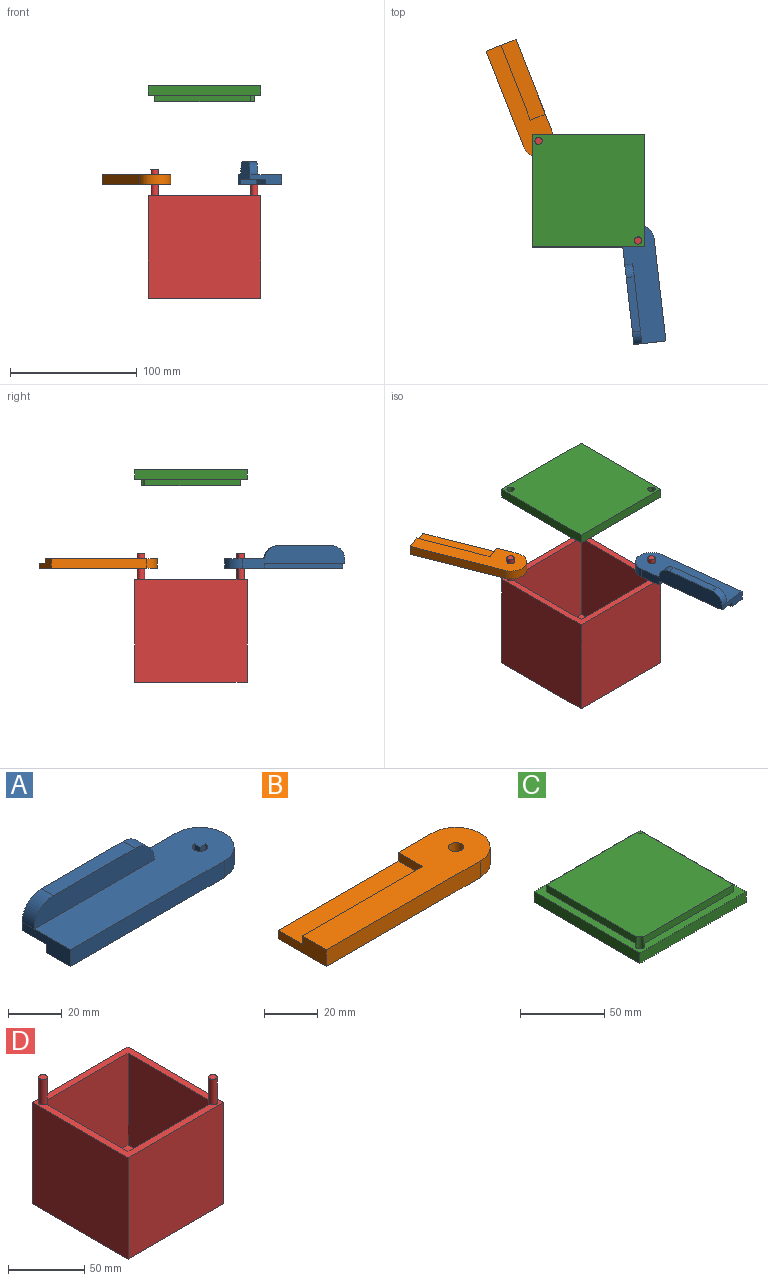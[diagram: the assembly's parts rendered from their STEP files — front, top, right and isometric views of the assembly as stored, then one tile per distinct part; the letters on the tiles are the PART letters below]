
ASSEMBLY  parts=4 mates=3
PART A: 16 faces, bbox 94x25.4x17.8 mm
  f0: plane 25.4x7.62mm, normal (-1,0,0), area 145.2mm2, adj f3,f4,f5,f6,f11,f13,f14
  f1: plane 63.5x10.16mm, normal (0,-1,0), area 600.9mm2, adj f2,f3,f14,f15
  f2: plane 43.18x6.35mm, normal (0,0,1), area 274.2mm2, adj f1,f4,f14,f15
  f3: plane 93.98x25.4mm, normal (0,0,1), area 1895.2mm2, adj f0,f1,f4,f5,f7,f8,f9,f10
  f4: plane 81.28x17.78mm, normal (0,1,0), area 978.3mm2, adj f0,f2,f3,f6,f7,f11,f12,f14
  f5: plane 81.28x7.62mm, normal (0,-1,0), area 619.4mm2, adj f0,f3,f6,f7
  f6: plane 93.98x25.4mm, normal (0,0,-1), area 1492mm2, adj f0,f4,f5,f7,f8,f9,f10,f12
  f7: cylinder r=12.7mm len=25.4mm, axis (0,0,1), area 304mm2, adj f3,f4,f5,f6
  f8: plane 7.62x2.87mm, normal (-1,0,0), area 21.9mm2, adj f3,f6,f9,f10
  f9: cylinder r=2.87mm len=7.62mm, axis (0,0,1), area 103.1mm2, adj f3,f6,f8,f10
  f10: plane 7.62x2.87mm, normal (0,-1,0), area 21.9mm2, adj f3,f6,f8,f9
  f11: plane 63.5x12.7mm, normal (0,0,-1), area 806.4mm2, adj f0,f4,f12,f13
  f12: plane 12.7x3.81mm, normal (-1,0,0), area 48.4mm2, adj f4,f6,f11,f13
  f13: plane 63.5x3.81mm, normal (0,1,0), area 241.9mm2, adj f0,f6,f11,f12
  f14: cylinder r=10.16mm len=10.16mm, axis (0,1,0), area 101.3mm2, adj f0,f1,f2,f4
  f15: cylinder r=10.16mm len=10.16mm, axis (0,1,0), area 101.3mm2, adj f1,f2,f3,f4
PART B: 10 faces, bbox 94x25.4x7.6 mm
  f0: plane 25.4x7.62mm, normal (-1,0,0), area 145.2mm2, adj f1,f2,f3,f4,f7,f9
  f1: plane 93.98x25.4mm, normal (0,0,1), area 1485.5mm2, adj f0,f2,f3,f5,f6,f8,f9
  f2: plane 81.28x7.62mm, normal (0,-1,0), area 619.4mm2, adj f0,f1,f4,f5
  f3: plane 81.28x7.62mm, normal (0,1,0), area 377.4mm2, adj f0,f1,f4,f5,f7,f8
  f4: plane 93.98x25.4mm, normal (0,0,-1), area 2291.9mm2, adj f0,f2,f3,f5,f6
  f5: cylinder r=12.7mm len=25.4mm, axis (0,0,1), area 304mm2, adj f1,f2,f3,f4
  f6: cylinder r=2.87mm len=7.62mm, axis (0,0,1), area 137.6mm2, adj f1,f4
  f7: plane 63.5x12.7mm, normal (0,0,1), area 806.4mm2, adj f0,f3,f8,f9
  f8: plane 12.7x3.81mm, normal (-1,0,0), area 48.4mm2, adj f1,f3,f7,f9
  f9: plane 63.5x3.81mm, normal (0,1,0), area 241.9mm2, adj f0,f1,f7,f8
PART C: 13 faces, bbox 88.9x88.9x12.7 mm
  f0: plane 88.9x88.9mm, normal (0,0,1), area 1664.4mm2, adj f1,f2,f3,f4,f6,f7,f8,f9
  f1: plane 88.9x7.62mm, normal (1,0,0), area 677.4mm2, adj f0,f2,f4,f5
  f2: plane 88.9x7.62mm, normal (0,1,0), area 677.4mm2, adj f0,f1,f3,f5
  f3: plane 88.9x7.62mm, normal (-1,0,0), area 677.4mm2, adj f0,f2,f4,f5
  f4: plane 88.9x7.62mm, normal (0,-1,0), area 677.4mm2, adj f0,f1,f3,f5
  f5: plane 88.9x88.9mm, normal (0,0,-1), area 7851.4mm2, adj f1,f2,f3,f4,f11,f12
  f6: plane 75.87x5.08mm, normal (0,-1,0), area 385.4mm2, adj f0,f7,f10,f11
  f7: plane 75.87x5.08mm, normal (1,0,0), area 385.4mm2, adj f0,f6,f10,f12
  f8: plane 75.87x5.08mm, normal (0,1,0), area 385.4mm2, adj f0,f9,f10,f12
  f9: plane 75.87x5.08mm, normal (-1,0,0), area 385.4mm2, adj f0,f8,f10,f11
  f10: plane 78.74x78.74mm, normal (0,0,1), area 6187mm2, adj f6,f7,f8,f9,f11,f12
  f11: cylinder r=2.87mm len=12.7mm, axis (0,0,1), area 160.3mm2, adj f0,f5,f6,f9,f10
  f12: cylinder r=2.87mm len=12.7mm, axis (0,0,1), area 160.5mm2, adj f0,f5,f7,f8,f10
PART D: 17 faces, bbox 88.9x88.9x101.6 mm
  f0: plane 75.87x73.66mm, normal (0,1,0), area 5588.6mm2, adj f7,f9,f10,f13
  f1: plane 75.87x73.66mm, normal (-1,0,0), area 5588.6mm2, adj f8,f9,f10,f13
  f2: plane 88.9x81.28mm, normal (-1,0,0), area 7225.8mm2, adj f3,f5,f6,f9
  f3: plane 88.9x81.28mm, normal (0,-1,0), area 7225.8mm2, adj f2,f4,f6,f9
  f4: plane 88.9x81.28mm, normal (1,0,0), area 7225.8mm2, adj f3,f5,f6,f9
  f5: plane 88.9x81.28mm, normal (0,1,0), area 7225.8mm2, adj f2,f4,f6,f9
  f6: plane 88.9x88.9mm, normal (0,0,-1), area 7903.2mm2, adj f2,f3,f4,f5
  f7: plane 75.87x73.66mm, normal (1,0,0), area 5588.3mm2, adj f0,f9,f10,f11
  f8: plane 75.87x73.66mm, normal (0,-1,0), area 5588.3mm2, adj f1,f9,f10,f11
  f9: plane 88.9x88.9mm, normal (0,0,1), area 1664.4mm2, adj f0,f1,f2,f3,f4,f5,f7,f8
  f10: plane 78.74x78.74mm, normal (0,0,1), area 6187mm2, adj f0,f1,f7,f8,f11,f13,f14,f15
  f11: cylinder r=2.87mm len=93.98mm, axis (0,0,-1), area 699.4mm2, adj f7,f8,f9,f10,f12
  f12: plane 5.75x5.75mm, normal (0,0,1), area 25.9mm2, adj f11
  f13: cylinder r=2.87mm len=93.98mm, axis (0,0,-1), area 697.9mm2, adj f0,f1,f9,f10,f14,f15,f16
  f14: plane 93.98x0.01mm, normal (-1,0,0), area 0.5mm2, adj f10,f13,f15,f16
  f15: plane 93.98x0.01mm, normal (0,1,0), area 0.5mm2, adj f10,f13,f14,f16
  f16: plane 5.74x5.74mm, normal (0,0,1), area 25.9mm2, adj f13,f14,f15
PLACE A rot(axis=(0,0,1),96.6deg) t=(-75.38,-146.83,49.12)mm
PLACE B rot(axis=(0,0,-1),68.7deg) t=(-173.55,10.14,49.12)mm
PLACE C rot(axis=(0,1,0),180deg) t=(-119.39,-67.08,127.01)mm
PLACE D t=(-119.39,-67.08,-41.05)mm fixed
MATE slider C.f11 <-> D.f13  axis (0,0,1) through (-80.02,-106.45,127.01)mm
MATE revolute A.f9 <-> D.f13  axis (0,0,1) through (-80.02,-106.45,56.74)mm
MATE revolute B.f5 <-> D.f11  axis (0,0,1) through (-158.76,-27.71,56.74)mm
